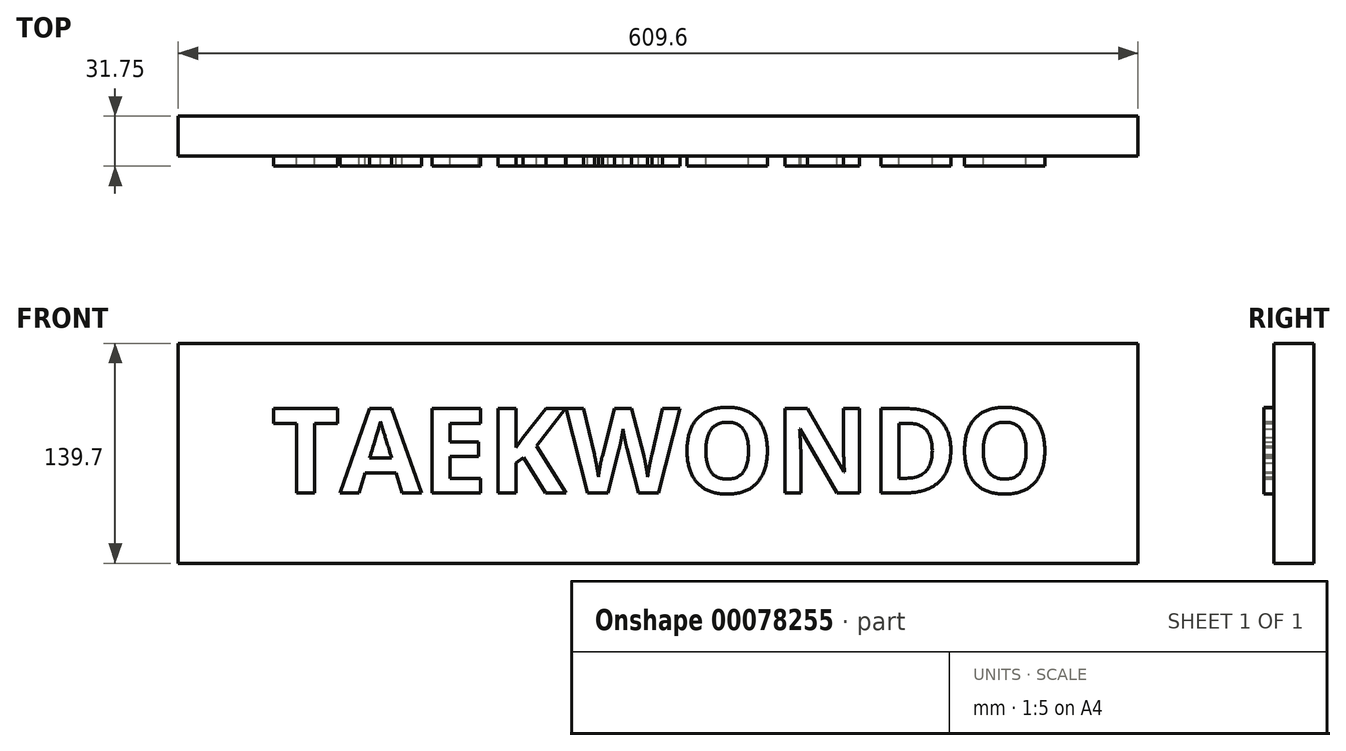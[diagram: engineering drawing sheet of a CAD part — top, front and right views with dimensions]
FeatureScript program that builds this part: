
annotation { "Feature Type Name" : "Feature", "Feature Type Description" : "" }
export const myFeature = defineFeature(function(context is Context, id is Id, definition is map)
    precondition{}
    {
        {
            var Q0;
            Q0=qCreatedBy(makeId("Top.planeOp"),FACE);
            var sketch = newSketch(context, id + "F0", { "sketchPlane" : qUnion([Q0])});
            skLineSegment(sketch, "E0.bottom", {"start": v(0, 0) * mm, "end": v(-609.6, 0) * mm});
            skLineSegment(sketch, "E0.top", {"start": v(0, 25.4) * mm, "end": v(-609.6, 25.4) * mm});
            skLineSegment(sketch, "E0.left", {"start": v(0, 0) * mm, "end": v(0, 25.4) * mm});
            skLineSegment(sketch, "E0.right", {"start": v(-609.6, 0) * mm, "end": v(-609.6, 25.4) * mm});
            skSolve(sketch);
        }
        {
            var Q0;
            Q0=makeQuery(id+"F0.imprint","IMPRINT",FACE,{"disambiguationData":[TD([[makeQuery(id+"F0.imprint","IMPRINT",EDGE,{"derivedFrom":sQuery(id+"F0.wireOp",EDGE,"E0.bottom")}),-1.0]])]});
            extrude(context, id + "F1", {"entities" : qUnion([Q0]), "depth" : 139.7 * mm});
        }
        {
            var Q0;
            Q0=makeQuery(id+"F1.opExtrude","SWEPT_FACE",FACE,{"disambiguationData":[OSD([sQuery(id+"F0.wireOp",EDGE,"E0.bottom")])]});
            var sketch = newSketch(context, id + "F2", { "sketchPlane" : qUnion([Q0])});
            skText(sketch, "E1", { "text": "TAEKWONDO", "fontName": "OpenSans-Bold.ttf"});
            skLineSegment(sketch, "E2", {"start": v(-550.4, 98.67) * mm, "end": v(-609.6, 98.67) * mm, "construction": true});
            skLineSegment(sketch, "E3", {"start": v(-59.2, 98.67) * mm, "end": v(0, 98.67) * mm, "construction": true});
            const initialGuessF2  = {"E1": [-0.5504, 0.04465, 1, 0, 0.05402]};
            skSetInitialGuess(sketch, initialGuessF2);
            skSolve(sketch);
        }
        {
            var Q0;
            Q0 = qSketchRegion(id + "F2", true);
            extrude(context, id + "F3", {"entities" : qUnion([Q0]), "operationType" : NewBodyOperationType.ADD, "depth" : 6.35 * mm});
        }
    });
